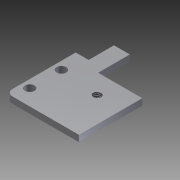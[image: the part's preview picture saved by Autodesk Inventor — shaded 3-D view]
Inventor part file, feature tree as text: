
AUTODESK INVENTOR PART (.ipt)
format: ipt  version: 2015 (Build 190159000, 159)  size: 108,544 bytes
history: native  units: mm
features: extrude x3, reference x2, hole x1
ambient origin geometry x8: Origin, YZ Plane, XZ Plane, XY Plane, X Axis, Y Axis, Z Axis, Center Point
bodies: Solid1 (feature_tree)
feature tree (6):
  extrude  "Extrusión1"  Depth=18.0mm
  extrude  "Extrusión2"  Depth=18.0mm
  hole  "Agujero1"  [1 undecoded]
  extrude  "Extrusión3"  Depth=5.0mm
  reference  "Referencia1"
  reference  "Referencia2"
note: 1 required parameter value undecoded (feature->parameter linkage not recoverable at this tier; creation-order binding heuristic only, values carry confidence <= 0.55)
